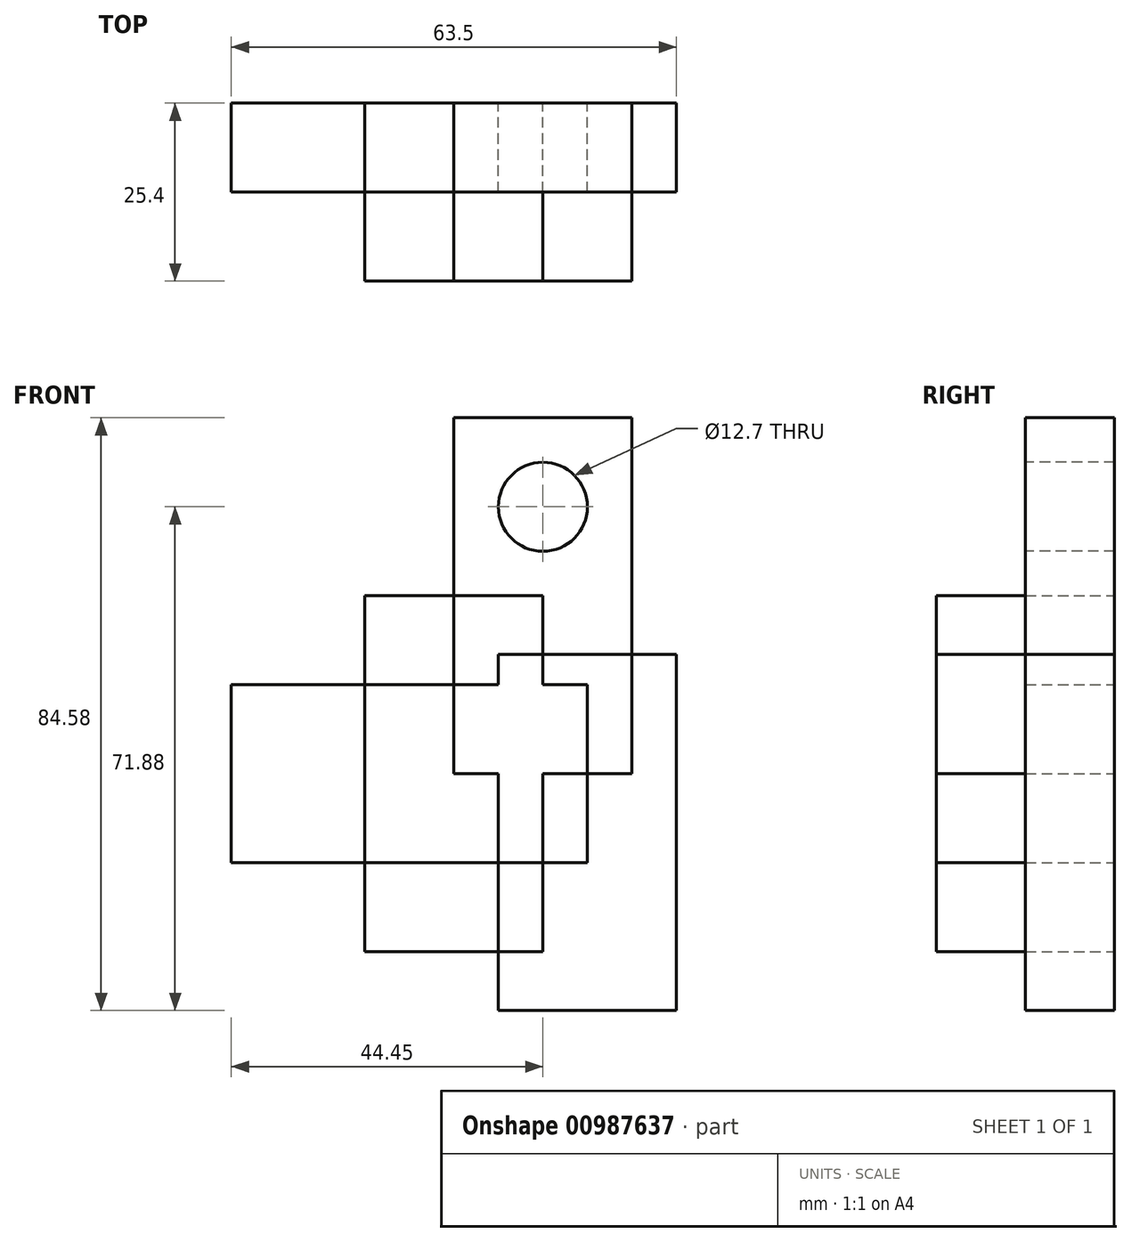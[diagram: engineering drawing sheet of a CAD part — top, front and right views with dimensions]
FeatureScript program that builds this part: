
annotation { "Feature Type Name" : "Feature", "Feature Type Description" : "" }
export const myFeature = defineFeature(function(context is Context, id is Id, definition is map)
    precondition{}
    {
        {
            var Q0;
            Q0=qCreatedBy(makeId("Front.planeOp"),FACE);
            var sketch = newSketch(context, id + "F0", { "sketchPlane" : qUnion([Q0])});
            skLineSegment(sketch, "E0.bottom", {"start": v(0, 50.8) * mm, "end": v(25.4, 50.8) * mm});
            skLineSegment(sketch, "E0.top", {"start": v(0, 0) * mm, "end": v(25.4, 0) * mm});
            skLineSegment(sketch, "E0.left", {"start": v(0, 50.8) * mm, "end": v(0, 0) * mm});
            skLineSegment(sketch, "E0.right", {"start": v(25.4, 50.8) * mm, "end": v(25.4, 0) * mm});
            skLineSegment(sketch, "E1.bottom", {"start": v(-31.75, 12.7) * mm, "end": v(19.05, 12.7) * mm});
            skLineSegment(sketch, "E1.top", {"start": v(-31.75, -12.7) * mm, "end": v(19.05, -12.7) * mm});
            skLineSegment(sketch, "E1.left", {"start": v(-31.75, 12.7) * mm, "end": v(-31.75, -12.7) * mm});
            skLineSegment(sketch, "E1.right", {"start": v(19.05, 12.7) * mm, "end": v(19.05, -12.7) * mm});
            skLineSegment(sketch, "E2.bottom", {"start": v(6.35, -33.78) * mm, "end": v(31.75, -33.78) * mm});
            skLineSegment(sketch, "E2.top", {"start": v(6.35, 17.02) * mm, "end": v(31.75, 17.02) * mm});
            skLineSegment(sketch, "E2.left", {"start": v(6.35, -33.78) * mm, "end": v(6.35, 17.02) * mm});
            skLineSegment(sketch, "E2.right", {"start": v(31.75, -33.78) * mm, "end": v(31.75, 17.02) * mm});
            skPoint(sketch, "E3.oppositeSnap0", {"position": v(12.7, 0) * mm});
            skLineSegment(sketch, "E3.bottom", {"start": v(-12.7, 25.4) * mm, "end": v(12.7, 25.4) * mm});
            skLineSegment(sketch, "E3.top", {"start": v(-12.7, -25.4) * mm, "end": v(12.7, -25.4) * mm});
            skLineSegment(sketch, "E3.left", {"start": v(-12.7, 25.4) * mm, "end": v(-12.7, -25.4) * mm});
            skLineSegment(sketch, "E3.right", {"start": v(12.7, 25.4) * mm, "end": v(12.7, -25.4) * mm});
            skSolve(sketch);
        }
        {
            var Q0;
            {var subQ5=sQuery(id+"F0.wireOp",EDGE,"E0.bottom");Q0=makeQuery(id+"F0.imprint","IMPRINT",FACE,{"disambiguationData":[TD([[makeQuery(id+"F0.imprint","IMPRINT",EDGE,{"derivedFrom":subQ5}),-1.0]])]});}
            var Q1;
            {var subQ0=sQuery(id+"F0.wireOp",EDGE,"E3.bottom");var subQ1=sQuery(id+"F0.wireOp",EDGE,"E0.left");var subQ2=makeQuery(id+"F0.imprint","INTERSECT",VERTEX,{"derivedFrom":[subQ1,subQ0]});Q1=makeQuery(id+"F0.imprint","IMPRINT",FACE,{"disambiguationData":[TD([[makeQuery(id+"F0.imprint","IMPRINT",EDGE,{"disambiguationData":[TD([[subQ2,-1.0]])],"derivedFrom":subQ1}),-1.0]])]});}
            var Q2;
            {var subQ15=sQuery(id+"F0.wireOp",EDGE,"E2.bottom");Q2=makeQuery(id+"F0.imprint","IMPRINT",FACE,{"disambiguationData":[TD([[makeQuery(id+"F0.imprint","IMPRINT",EDGE,{"derivedFrom":subQ15}),1.0]])]});}
            var Q3;
            {var subQ0=sQuery(id+"F0.wireOp",EDGE,"E3.left");var subQ1=sQuery(id+"F0.wireOp",EDGE,"E1.top");var subQ2=makeQuery(id+"F0.imprint","INTERSECT",VERTEX,{"derivedFrom":[subQ1,subQ0]});Q3=makeQuery(id+"F0.imprint","IMPRINT",FACE,{"disambiguationData":[TD([[makeQuery(id+"F0.imprint","IMPRINT",EDGE,{"disambiguationData":[TD([[subQ2,-1.0]])],"derivedFrom":subQ1}),-1.0]])]});}
            var Q4;
            {var subQ0=sQuery(id+"F0.wireOp",EDGE,"E1.left");Q4=makeQuery(id+"F0.imprint","IMPRINT",FACE,{"disambiguationData":[TD([[makeQuery(id+"F0.imprint","IMPRINT",EDGE,{"derivedFrom":subQ0}),1.0]])]});}
            extrude(context, id + "F1", {"entities" : qUnion([Q0, Q1, Q2, Q3, Q4]), "depth" : 12.7 * mm, "offsetDistance" : 25.4 * mm});
        }
        {
            var Q0;
            {var subQ0=sQuery(id+"F0.wireOp",EDGE,"E0.left");var subQ1=sQuery(id+"F0.wireOp",EDGE,"E0.top");var subQ2=makeQuery(id+"F0.imprint","INTERSECT",VERTEX,{"derivedFrom":[subQ1,subQ0]});Q0=makeQuery(id+"F0.imprint","IMPRINT",FACE,{"disambiguationData":[TD([[makeQuery(id+"F0.imprint","IMPRINT",EDGE,{"disambiguationData":[TD([[subQ2,-1.0]])],"derivedFrom":subQ1}),-1.0]])]});}
            var Q1;
            {var subQ0=sQuery(id+"F0.wireOp",EDGE,"E2.left");var subQ1=sQuery(id+"F0.wireOp",EDGE,"E1.top");var subQ2=makeQuery(id+"F0.imprint","INTERSECT",VERTEX,{"derivedFrom":[subQ1,subQ0]});Q1=makeQuery(id+"F0.imprint","IMPRINT",FACE,{"disambiguationData":[TD([[makeQuery(id+"F0.imprint","IMPRINT",EDGE,{"disambiguationData":[TD([[subQ2,-1.0]])],"derivedFrom":subQ1}),-1.0]])]});}
            var Q2;
            {var subQ0=sQuery(id+"F0.wireOp",EDGE,"E3.right");var subQ1=sQuery(id+"F0.wireOp",EDGE,"E0.top");var subQ2=makeQuery(id+"F0.imprint","INTERSECT",VERTEX,{"derivedFrom":[subQ1,subQ0]});Q2=makeQuery(id+"F0.imprint","IMPRINT",FACE,{"disambiguationData":[TD([[makeQuery(id+"F0.imprint","IMPRINT",EDGE,{"disambiguationData":[TD([[subQ2,-1.0]])],"derivedFrom":subQ1}),-1.0]])]});}
            var Q3;
            {var subQ3=sQuery(id+"F0.wireOp",EDGE,"E0.top");var subQ5=sQuery(id+"F0.wireOp",EDGE,"E0.right");var subQ6=makeQuery(id+"F0.imprint","INTERSECT",VERTEX,{"derivedFrom":[subQ3,subQ5]});Q3=makeQuery(id+"F0.imprint","IMPRINT",FACE,{"disambiguationData":[TD([[makeQuery(id+"F0.imprint","IMPRINT",EDGE,{"disambiguationData":[TD([[subQ6,1.0]])],"derivedFrom":subQ3}),1.0]])]});}
            var Q4;
            {var subQ7=sQuery(id+"F0.wireOp",EDGE,"E0.left");var subQ9=sQuery(id+"F0.wireOp",EDGE,"E3.bottom");var subQ10=makeQuery(id+"F0.imprint","INTERSECT",VERTEX,{"derivedFrom":[subQ7,subQ9]});Q4=makeQuery(id+"F0.imprint","IMPRINT",FACE,{"disambiguationData":[TD([[makeQuery(id+"F0.imprint","IMPRINT",EDGE,{"disambiguationData":[TD([[subQ10,-1.0]])],"derivedFrom":subQ7}),1.0]])]});}
            extrude(context, id + "F2", {"entities" : qUnion([Q0, Q1, Q2, Q3, Q4]), "depth" : 25.4 * mm, "offsetDistance" : 25.4 * mm});
        }
        {
            var Q0;
            Q0=makeQuery(id+"F1.opExtrude","CAP_FACE",FACE,{"disambiguationData":[OSD([sQuery(id+"F0.wireOp",EDGE,"E0.bottom"),sQuery(id+"F0.wireOp",EDGE,"E0.left"),sQuery(id+"F0.wireOp",EDGE,"E0.right"),sQuery(id+"F0.wireOp",EDGE,"E2.top"),sQuery(id+"F0.wireOp",EDGE,"E3.bottom"),sQuery(id+"F0.wireOp",EDGE,"E3.right")])],"isStart":false});
            var sketch = newSketch(context, id + "F3", { "sketchPlane" : qUnion([Q0])});
            skCircle(sketch, "E4", {"center": v(12.7, 38.1) * mm, "radius": 6.35 * mm});
            skSolve(sketch);
        }
        {
            var Q0;
            Q0=makeQuery(id+"F3.imprint","IMPRINT",FACE,{"disambiguationData":[TD([[makeQuery(id+"F3.imprint","IMPRINT",EDGE,{"derivedFrom":sQuery(id+"F3.wireOp",EDGE,"E4")}),1.0]])]});
            var Q1;
            Q1=sQuery(id+"F3.wireOp",EDGE,"E4");
            extrude(context, id + "F4", {"entities" : qUnion([Q0]), "operationType" : NewBodyOperationType.REMOVE, "surfaceEntities" : qUnion([Q1]), "oppositeDirection" : true, "depth" : 25.4 * mm, "offsetDistance" : 25.4 * mm});
        }
    });
